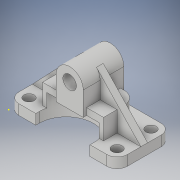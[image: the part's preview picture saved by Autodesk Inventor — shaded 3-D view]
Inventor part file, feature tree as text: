
AUTODESK INVENTOR PART (.ipt)
format: ipt  version: 2018 (Build 220112000, 112)  size: 247,296 bytes
history: native  units: in
note: dims shown in document units (in); Inventor stores cm internally (conversion verified against a paired STEP export)
features: sketch x13, extrude x8, fillet x8, hole x3, plane x1
ambient origin geometry x8: Origin, YZ Plane, XZ Plane, XY Plane, X Axis, Y Axis, Z Axis, Center Point
bodies: 实体1 (feature_tree)
feature tree (33):
  sketch  "草图1"  dims[d0=6.2992in d1=3.1496in d2=0.5906in d3=0.0in d4=0.5906in d5=0.5906in d6=0.5906in]
  extrude  "拉伸1"  Depth=3.1496in
  fillet  "圆角1"  Radius=0.5906in
  fillet  "圆角2"  Radius=0.5906in
  fillet  "圆角3"  Radius=0.5906in
  fillet  "圆角4"  Radius=0.5906in
  hole  "孔1"  [1 undecoded]
  extrude  "拉伸2"  Depth=1.1811in TaperAngle=0.0deg
  hole  "孔2"  [1 undecoded]
  extrude  "拉伸3"  Depth=1.7717in TaperAngle=0.0deg
  fillet  "圆角5"  Radius=0.7874in
  fillet  "圆角6"  Radius=0.7874in
  extrude  "拉伸4"  Depth=0.1969in TaperAngle=0.0deg
  extrude  "拉伸5"  Depth=0.3937in TaperAngle=0.0deg
  fillet  "圆角7"  [1 undecoded]
  fillet  "圆角8"  [1 undecoded]
  hole  "孔3"  [1 undecoded]
  extrude  "拉伸6"  [1 undecoded]
  extrude  "拉伸7"  [1 undecoded]
  sketch  "草图14"
  plane  "工作平面1"
  extrude  "拉伸9"  [1 undecoded]
  sketch  "草图2"  dims[d7=0.5906in]
  sketch  "草图4"  dims[d8=0.5906in d9=0.2362in d10=0.1575in d11=0.0787in d12=90.0deg d13=0.315in d14=0.8108in d19=0.5906in d20=0.0in]
  sketch  "草图5"  dims[d21=3.1496in d22=0.2362in d23=0.1575in d24=0.0787in d25=90.0deg d26=0.315in d27=0.8108in d32=1.1811in d33=0.0in]
  sketch  "草图6"  dims[d34=0.7874in d35=0.7874in]
  sketch  "草图7"  dims[d36=0.7874in d37=0.0in d43=1.7717in d44=0.0in d45=0.7874in d46=0.7874in]
  sketch  "草图8"  dims[d47=0.7874in d48=0.2362in d49=0.1575in d50=0.0787in d51=90.0deg d52=0.7874in d53=0.0in d54=0.1969in d55=0.0in]
  sketch  "草图9"  dims[d56=0.1969in d57=0.0in d60=0.3937in d61=0.0in]
  sketch  "草图10"
  sketch  "草图11"
  sketch  "草图12"
  sketch  "草图16"
note: 8 required parameter values undecoded (feature->parameter linkage not recoverable at this tier; creation-order binding heuristic only, values carry confidence <= 0.55)
